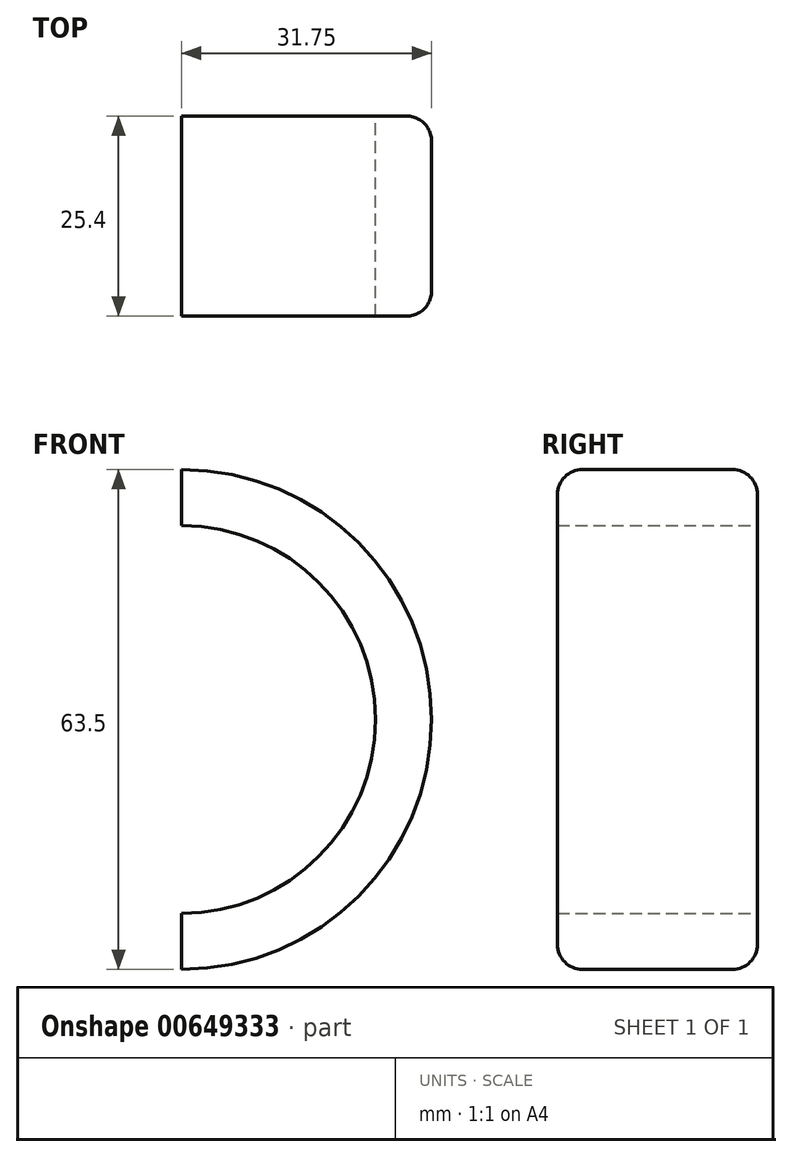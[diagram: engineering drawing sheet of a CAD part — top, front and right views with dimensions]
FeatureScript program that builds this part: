
annotation { "Feature Type Name" : "Feature", "Feature Type Description" : "" }
export const myFeature = defineFeature(function(context is Context, id is Id, definition is map)
    precondition{}
    {
        {
            var Q0;
            Q0=qCreatedBy(makeId("Front.planeOp"),FACE);
            var sketch = newSketch(context, id + "F0", { "sketchPlane" : qUnion([Q0])});
            skCircle(sketch, "E0", {"center": v(0, 0) * mm, "radius": 24.64 * mm});
            skCircle(sketch, "E1", {"center": v(0, 0) * mm, "radius": 31.75 * mm});
            skSolve(sketch);
        }
        {
            var Q0;
            Q0=makeQuery(id+"F0.imprint","IMPRINT",FACE,{"disambiguationData":[TD([[makeQuery(id+"F0.imprint","IMPRINT",EDGE,{"derivedFrom":sQuery(id+"F0.wireOp",EDGE,"E0")}),-1.0]])]});
            extrude(context, id + "F1", {"entities" : qUnion([Q0]), "endBound" : BoundingType.SYMMETRIC, "depth" : 25.4 * mm, "offsetDistance" : 25.4 * mm});
        }
        {
            var Q0;
            Q0=makeQuery(id+"F1.opExtrude","CAP_EDGE",EDGE,{"disambiguationData":[OSD([sQuery(id+"F0.wireOp",EDGE,"E1")])],"isStart":false});
            var Q1;
            Q1=makeQuery(id+"F1.opExtrude","CAP_EDGE",EDGE,{"disambiguationData":[OSD([sQuery(id+"F0.wireOp",EDGE,"E1")])],"isStart":true});
            fillet(context, id + "F2", {"entities" : qUnion([Q0, Q1]), "radius" : 3.17 * mm, "tangentPropagation" : true, "allowEdgeOverflow" : false});
        }
        {
            var Q0;
            Q0=qCreatedBy(makeId("Front.planeOp"),FACE);
            var sketch = newSketch(context, id + "F3", { "sketchPlane" : qUnion([Q0])});
            skLineSegment(sketch, "E2.bottom", {"start": v(0, 34.32) * mm, "end": v(-32.75, 34.32) * mm});
            skLineSegment(sketch, "E2.top", {"start": v(0, -34.72) * mm, "end": v(-32.75, -34.72) * mm});
            skLineSegment(sketch, "E2.left", {"start": v(0, 34.32) * mm, "end": v(0, -34.72) * mm});
            skLineSegment(sketch, "E2.right", {"start": v(-32.75, 34.32) * mm, "end": v(-32.75, -34.72) * mm});
            skSolve(sketch);
        }
        {
            var Q0;
            Q0=makeQuery(id+"F3.imprint","IMPRINT",FACE,{"disambiguationData":[TD([[makeQuery(id+"F3.imprint","IMPRINT",EDGE,{"derivedFrom":sQuery(id+"F3.wireOp",EDGE,"E2.bottom")}),1.0]])]});
            extrude(context, id + "F4", {"entities" : qUnion([Q0]), "operationType" : NewBodyOperationType.REMOVE, "endBound" : BoundingType.SYMMETRIC, "oppositeDirection" : true, "depth" : 31.75 * mm, "offsetDistance" : 25.4 * mm});
        }
    });
